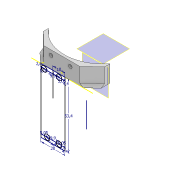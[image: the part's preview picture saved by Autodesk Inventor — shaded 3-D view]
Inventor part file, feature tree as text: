
AUTODESK INVENTOR PART (.ipt)
format: ipt  version: 2021 (Build 250183000, 183)  size: 236,544 bytes
history: native  units: mm
features: sketch x11, extrude x9, plane x2, other x1, chamfer x1
ambient origin geometry x8: Origin, YZ Plane, XZ Plane, XY Plane, X Axis, Y Axis, Z Axis, Center Point
bodies: Body1 (feature_tree), Body2 (feature_tree)
feature tree (24):
  other  "Sólido1"
  plane  "Plano de trabajo1"
  extrude  "Extrusión2"  Depth=3.0mm
  plane  "Plano de trabajo2"
  extrude  "Extrusión3"  Depth=2.0mm
  extrude  "Extrusión4"  Depth=50.0mm
  extrude  "Extrusión5"  Depth=15.0mm
  extrude  "Extrusión6"  Depth=12.0mm TaperAngle=0.0deg
  extrude  "Extrusión7"  Depth=8.0mm
  extrude  "Extrusión8"  Depth=3.0mm
  extrude  "Extrusión9"  Depth=12.0mm TaperAngle=0.0deg
  sketch  "Boceto11"  dims[d36=8.0mm d37=0.0mm d38=20.5mm]
  chamfer  "Chaflán1"  Distance=2.0mm
  extrude  "Extrusión10"  Depth=20.5mm
  sketch  "Boceto14"  dims[d40=20.2mm d41=20.2mm d43=7.0mm d44=6.0mm d45=14.5mm d46=0.0mm d47=5.0mm d48=0.0mm d49=10.0mm d50=14.0mm d51=0.0mm d52=2.0mm d53=2.0mm d54=45.0deg d55=100.0mm d56=0.0mm d59=10.0mm d60=53.4mm d61=20.0mm d68=2.6mm d69=5.05mm d70=9.9mm d71=5.05mm d72=4.4mm d73=4.4mm d74=2.6mm d75=5.05mm d76=9.9mm d77=5.05mm d78=4.4mm d79=4.4mm]
  sketch  "Boceto2"  dims[d15=3.0mm d16=3.0mm]
  sketch  "Boceto4"  dims[d17=12.0mm d18=0.0mm d19=2.0mm]
  sketch  "Boceto5"  dims[d20=20.0mm d21=50.0mm]
  sketch  "Boceto6"  dims[d22=100.0mm d23=15.0mm]
  sketch  "Boceto7"  dims[d24=15.0mm d25=12.0mm d26=0.0mm]
  sketch  "Boceto8"  dims[d27=8.0mm d28=8.0mm]
  sketch  "Boceto9"  dims[d29=16.0mm d30=3.0mm]
  sketch  "Boceto10"  dims[d31=3.0mm d32=12.0mm d33=0.0mm d34=2.0mm d35=0.0mm]
  sketch  "Boceto12"  dims[d39=20.5mm]
